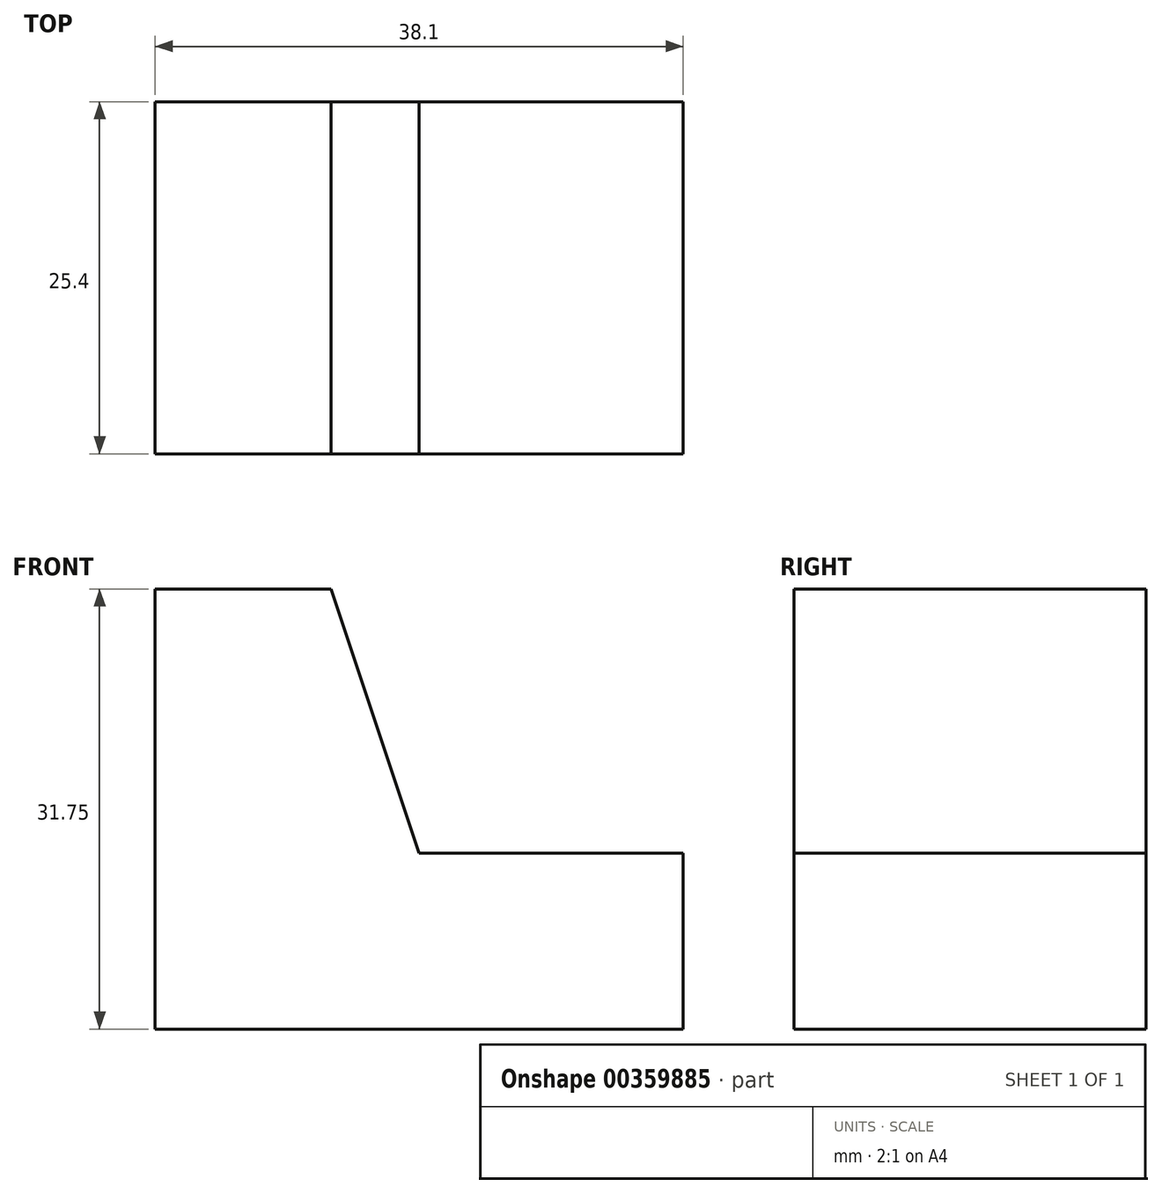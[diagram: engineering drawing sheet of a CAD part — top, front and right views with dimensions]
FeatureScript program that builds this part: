
annotation { "Feature Type Name" : "Feature", "Feature Type Description" : "" }
export const myFeature = defineFeature(function(context is Context, id is Id, definition is map)
    precondition{}
    {
        {
            var Q0;
            Q0=qCreatedBy(makeId("Front.planeOp"),FACE);
            var sketch = newSketch(context, id + "F0", { "sketchPlane" : qUnion([Q0])});
            skLineSegment(sketch, "E0", {"start": v(0, 0) * mm, "end": v(38.1, 0) * mm});
            skLineSegment(sketch, "E1", {"start": v(38.1, 0) * mm, "end": v(38.1, 31.75) * mm});
            skLineSegment(sketch, "E2", {"start": v(38.1, 31.75) * mm, "end": v(0, 31.75) * mm});
            skLineSegment(sketch, "E3", {"start": v(0, 31.75) * mm, "end": v(0, 0) * mm});
            skSolve(sketch);
        }
        {
            var Q0;
            Q0 = qSketchRegion(id + "F0", true);
            extrude(context, id + "F1", {"entities" : qUnion([Q0]), "depth" : 25.4 * mm});
        }
        {
            var Q0;
            Q0=makeQuery(id+"F1.opExtrude","CAP_FACE",FACE,{"disambiguationData":[OSD([sQuery(id+"F0.wireOp",EDGE,"E0"),sQuery(id+"F0.wireOp",EDGE,"E1"),sQuery(id+"F0.wireOp",EDGE,"E2"),sQuery(id+"F0.wireOp",EDGE,"E3")])],"isStart":false});
            var sketch = newSketch(context, id + "F2", { "sketchPlane" : qUnion([Q0])});
            skLineSegment(sketch, "E4", {"start": v(12.7, 31.75) * mm, "end": v(19.05, 12.7) * mm});
            skPoint(sketch, "E4.endSnap0", {"position": v(19.05, 31.75) * mm});
            skLineSegment(sketch, "E5", {"start": v(19.05, 12.7) * mm, "end": v(38.1, 12.7) * mm});
            skSolve(sketch);
        }
        {
            var Q0;
            Q0 = qSketchRegion(id + "F2", true);
            var Q1;
            {var subQ0=sQuery(id+"F2.wireOp",EDGE,"E4");Q1=makeQuery(id+"F2.imprint","IMPRINT",FACE,{"disambiguationData":[TD([[makeQuery(id+"F2.imprint","IMPRINT",EDGE,{"derivedFrom":subQ0}),1.0]])]});}
            extrude(context, id + "F3", {"entities" : qUnion([Q0, Q1]), "operationType" : NewBodyOperationType.REMOVE, "oppositeDirection" : true, "depth" : 25.4 * mm});
        }
    });
